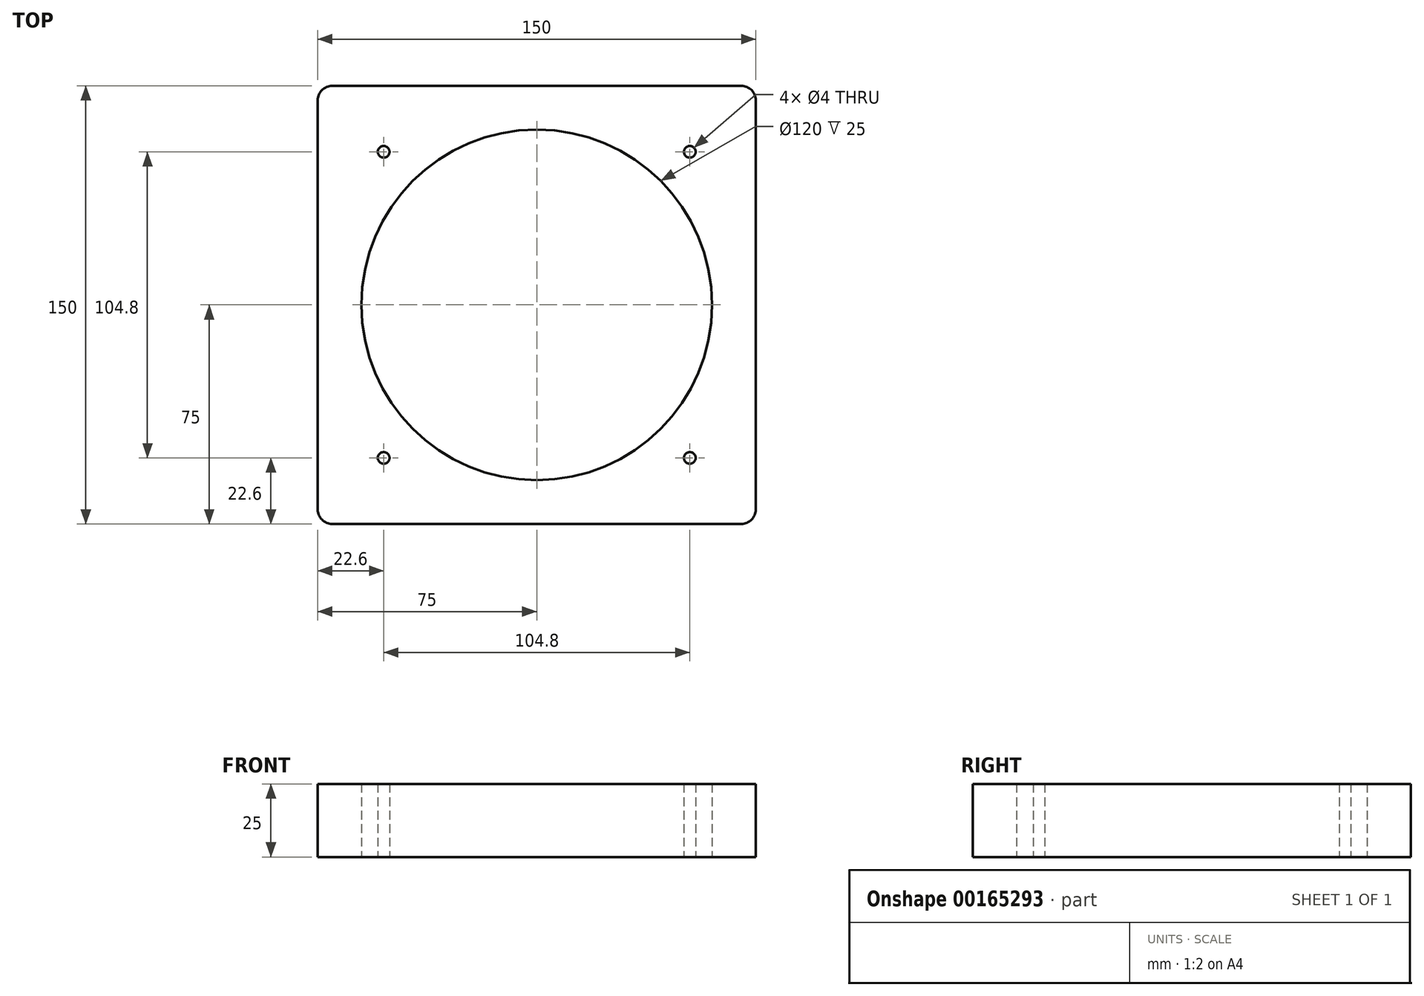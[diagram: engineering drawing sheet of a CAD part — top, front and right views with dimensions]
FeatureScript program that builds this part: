
annotation { "Feature Type Name" : "Feature", "Feature Type Description" : "" }
export const myFeature = defineFeature(function(context is Context, id is Id, definition is map)
    precondition{}
    {
        {
            var Q0;
            Q0=qCreatedBy(makeId("Top.planeOp"),FACE);
            var sketch = newSketch(context, id + "F0", { "sketchPlane" : qUnion([Q0])});
            skCircle(sketch, "E0", {"center": v(0, 0) * mm, "radius": 60 * mm});
            skCircle(sketch, "E1", {"center": v(-52.4, 52.4) * mm, "radius": 2 * mm});
            skCircle(sketch, "E2", {"center": v(52.4, 52.4) * mm, "radius": 2 * mm});
            skCircle(sketch, "E3", {"center": v(52.4, -52.4) * mm, "radius": 2 * mm});
            skCircle(sketch, "E4", {"center": v(-52.4, -52.4) * mm, "radius": 2 * mm});
            skLineSegment(sketch, "E5.bottom", {"start": v(-70, 75) * mm, "end": v(70, 75) * mm});
            skLineSegment(sketch, "E5.top", {"start": v(-70, -75) * mm, "end": v(70, -75) * mm});
            skLineSegment(sketch, "E5.left", {"start": v(-75, 70) * mm, "end": v(-75, -70) * mm});
            skLineSegment(sketch, "E5.right", {"start": v(75, 70) * mm, "end": v(75, -70) * mm});
            skPoint(sketch, "E6.visualSharp", {"position": v(-75, 75) * mm});
            skArc(sketch, "E6.filletArc", {"start": v(-70, 75) * mm, "mid": v(-73.54, 73.54) * mm, "end": v(-75, 70) * mm});
            skPoint(sketch, "E7.visualSharp", {"position": v(75, 75) * mm});
            skArc(sketch, "E7.filletArc", {"start": v(75, 70) * mm, "mid": v(73.54, 73.54) * mm, "end": v(70, 75) * mm});
            skPoint(sketch, "E8.visualSharp", {"position": v(75, -75) * mm});
            skArc(sketch, "E8.filletArc", {"start": v(70, -75) * mm, "mid": v(73.54, -73.54) * mm, "end": v(75, -70) * mm});
            skPoint(sketch, "E9.visualSharp", {"position": v(-75, -75) * mm});
            skArc(sketch, "E9.filletArc", {"start": v(-75, -70) * mm, "mid": v(-73.54, -73.54) * mm, "end": v(-70, -75) * mm});
            skSolve(sketch);
        }
        {
            var Q0;
            Q0=makeQuery(id+"F0.imprint","IMPRINT",FACE,{"disambiguationData":[TD([[makeQuery(id+"F0.imprint","IMPRINT",EDGE,{"derivedFrom":sQuery(id+"F0.wireOp",EDGE,"E1")}),-1.0]])]});
            var Q1;
            Q1=makeQuery(id+"F0.imprint","IMPRINT",FACE,{"disambiguationData":[TD([[makeQuery(id+"F0.imprint","IMPRINT",EDGE,{"derivedFrom":sQuery(id+"F0.wireOp",EDGE,"E2")}),-1.0]])]});
            var Q2;
            Q2=makeQuery(id+"F0.imprint","IMPRINT",FACE,{"disambiguationData":[TD([[makeQuery(id+"F0.imprint","IMPRINT",EDGE,{"derivedFrom":sQuery(id+"F0.wireOp",EDGE,"E4")}),-1.0]])]});
            var Q3;
            Q3=makeQuery(id+"F0.imprint","IMPRINT",FACE,{"disambiguationData":[TD([[makeQuery(id+"F0.imprint","IMPRINT",EDGE,{"derivedFrom":sQuery(id+"F0.wireOp",EDGE,"E3")}),-1.0]])]});
            var Q4;
            Q4=sQuery(id+"F0.wireOp",EDGE,"E2");
            var Q5;
            Q5=sQuery(id+"F0.wireOp",EDGE,"E3");
            var Q6;
            Q6=sQuery(id+"F0.wireOp",EDGE,"E4");
            var Q7;
            Q7=sQuery(id+"F0.wireOp",EDGE,"E1");
            var Q8;
            Q8=sQuery(id+"F0.wireOp",EDGE,"E0");
            var Q9;
            Q9=sQuery(id+"F0.wireOp",EDGE,"E5.left");
            var Q10;
            Q10=sQuery(id+"F0.wireOp",EDGE,"E5.bottom");
            var Q11;
            Q11=sQuery(id+"F0.wireOp",EDGE,"E5.right");
            var Q12;
            Q12=sQuery(id+"F0.wireOp",EDGE,"E5.top");
            extrude(context, id + "F1", {"entities" : qUnion([Q0, Q1, Q2, Q3]), "surfaceEntities" : qUnion([Q4, Q5, Q6, Q7, Q8, Q9, Q10, Q11, Q12]), "depth" : 25 * mm});
        }
    });
